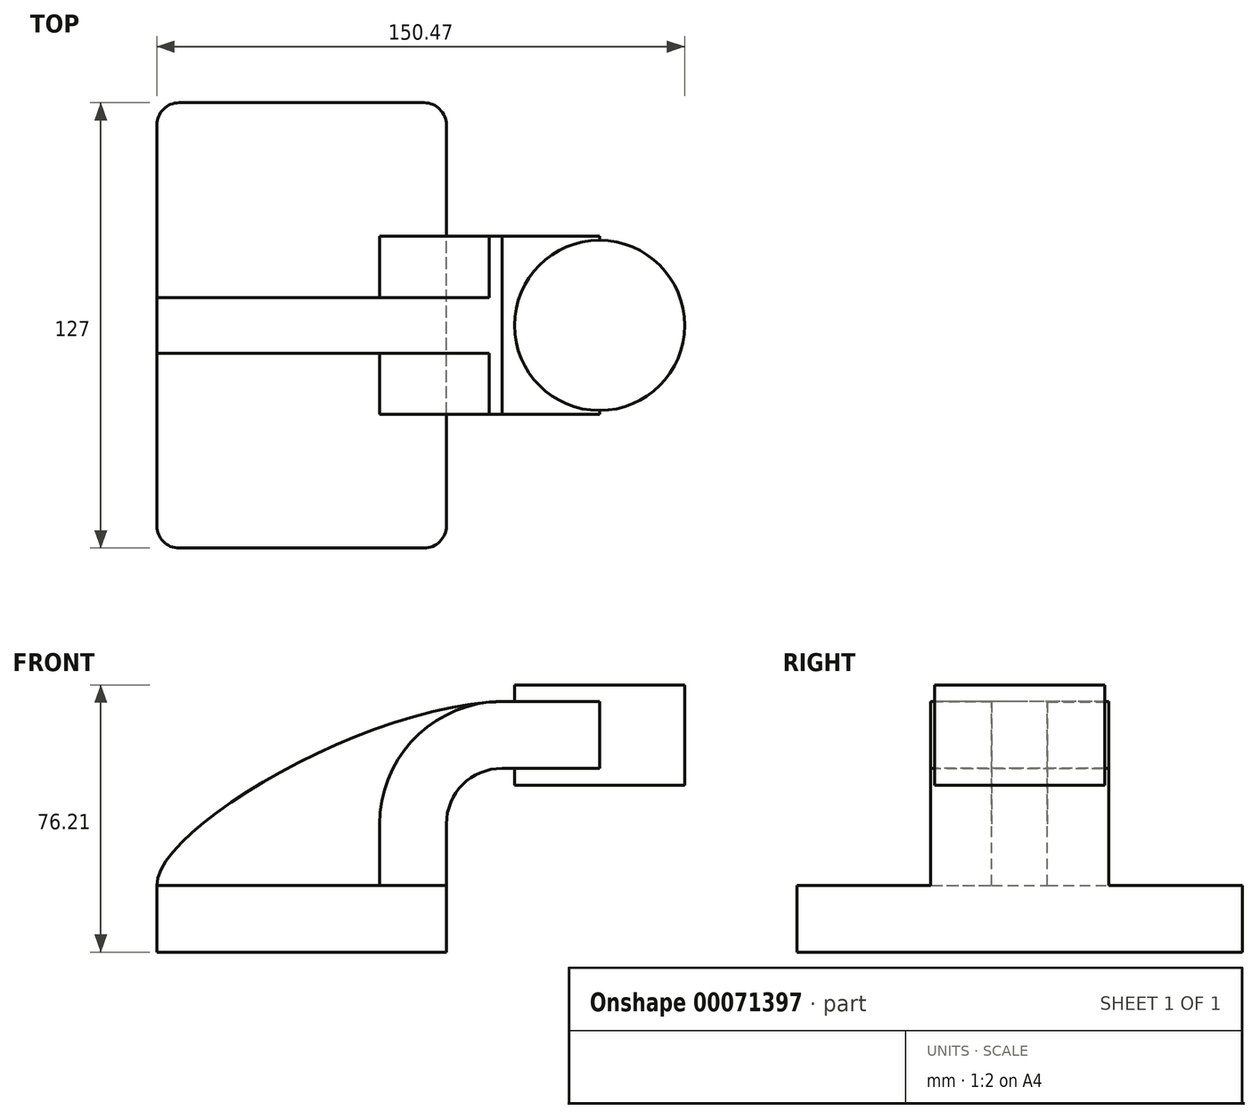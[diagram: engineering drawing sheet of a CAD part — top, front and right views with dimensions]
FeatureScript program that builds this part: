
annotation { "Feature Type Name" : "Feature", "Feature Type Description" : "" }
export const myFeature = defineFeature(function(context is Context, id is Id, definition is map)
    precondition{}
    {
        {
            var Q0;
            Q0=qCreatedBy(makeId("Front.planeOp"),FACE);
            var sketch = newSketch(context, id + "F0", { "sketchPlane" : qUnion([Q0])});
            skLineSegment(sketch, "E0.rect.bottom", {"start": v(41.28, -9.52) * mm, "end": v(-41.28, -9.53) * mm});
            skLineSegment(sketch, "E0.rect.top", {"start": v(41.28, 9.53) * mm, "end": v(-41.28, 9.53) * mm});
            skLineSegment(sketch, "E0.rect.left", {"start": v(41.28, -9.52) * mm, "end": v(41.28, 9.53) * mm});
            skLineSegment(sketch, "E0.rect.right", {"start": v(-41.28, -9.53) * mm, "end": v(-41.28, 9.53) * mm});
            skPoint(sketch, "E0.rect.middle", {"position": v(0, 0) * mm});
            skLineSegment(sketch, "E1.rect.bottom", {"start": v(58.39, 66.68) * mm, "end": v(109.19, 66.68) * mm});
            skLineSegment(sketch, "E1.rect.top", {"start": v(58.39, 38.1) * mm, "end": v(109.19, 38.1) * mm});
            skLineSegment(sketch, "E1.rect.left", {"start": v(58.39, 66.68) * mm, "end": v(58.39, 38.1) * mm});
            skLineSegment(sketch, "E1.rect.right", {"start": v(109.19, 66.68) * mm, "end": v(109.19, 38.1) * mm});
            skPoint(sketch, "E1.rect.middle", {"position": v(83.79, 52.39) * mm});
            skLineSegment(sketch, "E2", {"start": v(41.28, 9.53) * mm, "end": v(41.28, 27) * mm});
            skArc(sketch, "E3", {"start": v(41.27, 27) * mm, "mid": v(45.92, 38.23) * mm, "end": v(57.15, 42.88) * mm});
            skLineSegment(sketch, "E4", {"start": v(57.15, 42.88) * mm, "end": v(84.94, 42.88) * mm});
            skLineSegment(sketch, "E5.0", {"start": v(57.15, 61.93) * mm, "end": v(84.94, 61.93) * mm});
            skArc(sketch, "E5.1", {"start": v(22.23, 27) * mm, "mid": v(32.45, 51.7) * mm, "end": v(57.15, 61.93) * mm});
            skLineSegment(sketch, "E5.2", {"start": v(22.22, 9.53) * mm, "end": v(22.22, 27) * mm});
            skLineSegment(sketch, "E6", {"start": v(84.94, 38.1) * mm, "end": v(84.94, 66.68) * mm});
            skPoint(sketch, "E6.startSnap0", {"position": v(83.79, 38.1) * mm});
            skFitSpline(sketch, "E7", {"points": [v(-41.28, 9.53) * mm, v(57.15, 61.93) * mm], "startDerivative": vector(-0.83, 48.37) * mm, "endDerivative": vector(116.43, 3.1) * mm});
            skSolve(sketch);
        }
        {
            var Q0;
            Q0=makeQuery(id+"F0.imprint","IMPRINT",FACE,{"disambiguationData":[TD([[makeQuery(id+"F0.imprint","IMPRINT",EDGE,{"derivedFrom":sQuery(id+"F0.wireOp",EDGE,"E0.rect.bottom")}),-1.0]])]});
            extrude(context, id + "F1", {"entities" : qUnion([Q0]), "depth" : 127 * mm, "symmetric" : true});
        }
        {
            var Q0;
            {var subQ1=sQuery(id+"F0.wireOp",EDGE,"E2");Q0=makeQuery(id+"F0.imprint","IMPRINT",FACE,{"disambiguationData":[TD([[makeQuery(id+"F0.imprint","IMPRINT",EDGE,{"derivedFrom":subQ1}),1.0]])]});}
            var Q1;
            {var subQ0=sQuery(id+"F0.wireOp",EDGE,"E5.0");var subQ1=sQuery(id+"F0.wireOp",EDGE,"E1.rect.left");var subQ2=makeQuery(id+"F0.imprint","INTERSECT",VERTEX,{"derivedFrom":[subQ1,subQ0]});Q1=makeQuery(id+"F0.imprint","IMPRINT",FACE,{"disambiguationData":[TD([[makeQuery(id+"F0.imprint","IMPRINT",EDGE,{"disambiguationData":[TD([[subQ2,-1.0]])],"derivedFrom":subQ1}),1.0]])]});}
            extrude(context, id + "F2", {"entities" : qUnion([Q0, Q1]), "operationType" : NewBodyOperationType.ADD, "depth" : 50.8 * mm, "symmetric" : true});
        }
        {
            var Q0;
            {var subQ3=sQuery(id+"F0.wireOp",EDGE,"E5.2");Q0=makeQuery(id+"F0.imprint","IMPRINT",FACE,{"disambiguationData":[TD([[makeQuery(id+"F0.imprint","IMPRINT",EDGE,{"derivedFrom":subQ3}),1.0]])]});}
            extrude(context, id + "F3", {"entities" : qUnion([Q0]), "operationType" : NewBodyOperationType.ADD, "depth" : 15.88 * mm, "symmetric" : true});
        }
        {
            var Q0;
            {var subQ0=sQuery(id+"F0.wireOp",EDGE,"E1.rect.right");Q0=makeQuery(id+"F0.imprint","IMPRINT",FACE,{"disambiguationData":[TD([[makeQuery(id+"F0.imprint","IMPRINT",EDGE,{"derivedFrom":subQ0}),-1.0]])]});}
            var Q1;
            Q1=sQuery(id+"F0.wireOp",EDGE,"E6");
            revolve(context, id + "F4", {"operationType" : NewBodyOperationType.ADD, "entities" : qUnion([Q0]), "axis" : qUnion([Q1]), "revolveType" : RevolveType.FULL});
        }
        {
            var Q0;
            Q0=makeQuery(id+"F1.opExtrude","CAP_EDGE",EDGE,{"disambiguationData":[OSD([sQuery(id+"F0.wireOp",EDGE,"E0.rect.right")])],"isStart":false});
            var Q1;
            Q1=makeQuery(id+"F1.opExtrude","CAP_EDGE",EDGE,{"disambiguationData":[OSD([sQuery(id+"F0.wireOp",EDGE,"E0.rect.left")])],"isStart":false});
            var Q2;
            Q2=makeQuery(id+"F1.opExtrude","CAP_EDGE",EDGE,{"disambiguationData":[OSD([sQuery(id+"F0.wireOp",EDGE,"E0.rect.left")])],"isStart":true});
            var Q3;
            Q3=makeQuery(id+"F1.opExtrude","CAP_EDGE",EDGE,{"disambiguationData":[OSD([sQuery(id+"F0.wireOp",EDGE,"E0.rect.right")])],"isStart":true});
            fillet(context, id + "F5", {"entities" : qUnion([Q0, Q1, Q2, Q3]), "radius" : 6.35 * mm, "tangentPropagation" : true, "allowEdgeOverflow" : false});
        }
    });
